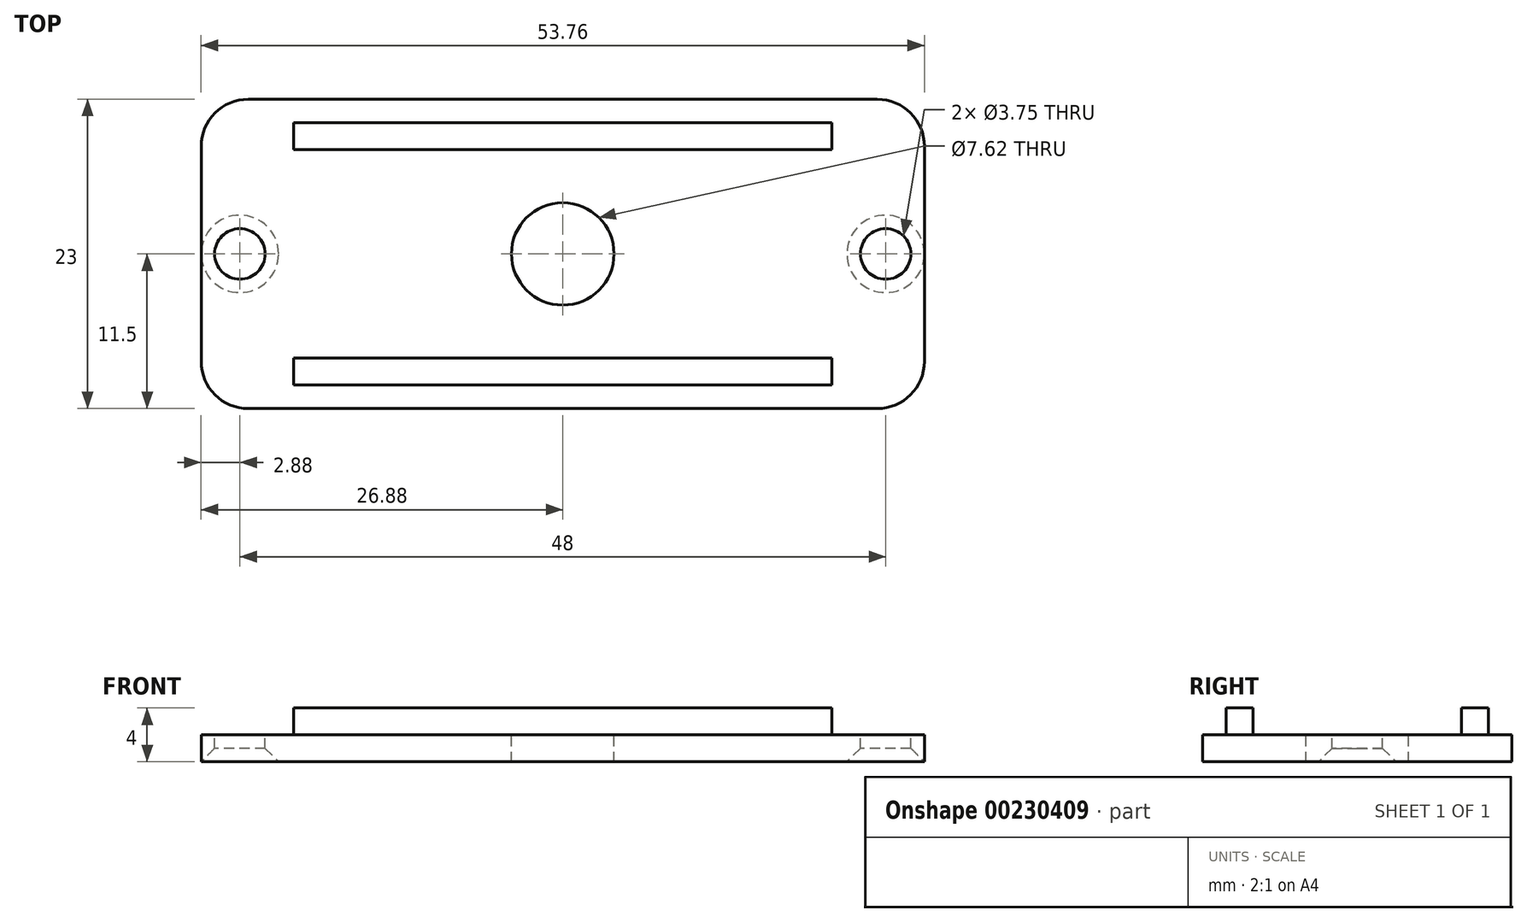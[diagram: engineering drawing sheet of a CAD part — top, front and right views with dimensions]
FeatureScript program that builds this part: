
annotation { "Feature Type Name" : "Feature", "Feature Type Description" : "" }
export const myFeature = defineFeature(function(context is Context, id is Id, definition is map)
    precondition{}
    {
        {
            var Q0;
            Q0=qCreatedBy(makeId("Top.planeOp"),FACE);
            var sketch = newSketch(context, id + "F0", { "sketchPlane" : qUnion([Q0])});
            skLineSegment(sketch, "E0.bottom", {"start": v(23.38, 11.5) * mm, "end": v(-23.37, 11.5) * mm});
            skLineSegment(sketch, "E0.top", {"start": v(23.38, -11.5) * mm, "end": v(-23.37, -11.5) * mm});
            skLineSegment(sketch, "E0.left", {"start": v(26.88, 8) * mm, "end": v(26.88, -8) * mm});
            skLineSegment(sketch, "E0.right", {"start": v(-26.87, 8) * mm, "end": v(-26.87, -8) * mm});
            skPoint(sketch, "E0.middle", {"position": v(0, 0) * mm});
            skPoint(sketch, "E1.visualSharp", {"position": v(-26.88, 11.5) * mm});
            skArc(sketch, "E1.filletArc", {"start": v(-23.37, 11.5) * mm, "mid": v(-25.85, 10.47) * mm, "end": v(-26.87, 8) * mm});
            skPoint(sketch, "E2.visualSharp", {"position": v(-26.87, -11.5) * mm});
            skArc(sketch, "E2.filletArc", {"start": v(-26.87, -8) * mm, "mid": v(-25.85, -10.47) * mm, "end": v(-23.37, -11.5) * mm});
            skPoint(sketch, "E3.visualSharp", {"position": v(26.88, -11.5) * mm});
            skArc(sketch, "E3.filletArc", {"start": v(23.38, -11.5) * mm, "mid": v(25.85, -10.47) * mm, "end": v(26.88, -8) * mm});
            skPoint(sketch, "E4.visualSharp", {"position": v(26.87, 11.5) * mm});
            skArc(sketch, "E4.filletArc", {"start": v(26.88, 8) * mm, "mid": v(25.85, 10.47) * mm, "end": v(23.38, 11.5) * mm});
            skSolve(sketch);
        }
        {
            var Q0;
            Q0=makeQuery(id+"F0.imprint","IMPRINT",FACE,{"disambiguationData":[TD([[makeQuery(id+"F0.imprint","IMPRINT",EDGE,{"derivedFrom":sQuery(id+"F0.wireOp",EDGE,"E0.bottom")}),1.0]])]});
            extrude(context, id + "F1", {"entities" : qUnion([Q0]), "depth" : 2 * mm});
        }
        {
            var Q0;
            Q0=makeQuery(id+"F1.opExtrude","CAP_FACE",FACE,{"disambiguationData":[OSD([sQuery(id+"F0.wireOp",EDGE,"E0.bottom"),sQuery(id+"F0.wireOp",EDGE,"E0.top"),sQuery(id+"F0.wireOp",EDGE,"E0.left"),sQuery(id+"F0.wireOp",EDGE,"E0.right"),sQuery(id+"F0.wireOp",EDGE,"E1.filletArc"),sQuery(id+"F0.wireOp",EDGE,"E2.filletArc"),sQuery(id+"F0.wireOp",EDGE,"E3.filletArc"),sQuery(id+"F0.wireOp",EDGE,"E4.filletArc")])],"isStart":false});
            var sketch = newSketch(context, id + "F2", { "sketchPlane" : qUnion([Q0])});
            skCircle(sketch, "E5", {"center": v(-24, 0) * mm, "radius": 1.88 * mm});
            skCircle(sketch, "E6", {"center": v(24, 0) * mm, "radius": 1.88 * mm});
            skSolve(sketch);
        }
        {
            var Q0;
            Q0 = qSketchRegion(id + "F2", true);
            extrude(context, id + "F3", {"entities" : qUnion([Q0]), "operationType" : NewBodyOperationType.REMOVE, "endBound" : BoundingType.THROUGH_ALL, "oppositeDirection" : true, "depth" : 25 * mm});
        }
        {
            var Q0;
            Q0=makeQuery(id+"F3.boolean.opBoolean","INTERSECT",EDGE,{"derivedFrom":[makeQuery(id+"F1.opExtrude","CAP_FACE",FACE,{"disambiguationData":[OSD([sQuery(id+"F0.wireOp",EDGE,"E0.bottom"),sQuery(id+"F0.wireOp",EDGE,"E0.top"),sQuery(id+"F0.wireOp",EDGE,"E0.left"),sQuery(id+"F0.wireOp",EDGE,"E0.right"),sQuery(id+"F0.wireOp",EDGE,"E1.filletArc"),sQuery(id+"F0.wireOp",EDGE,"E2.filletArc"),sQuery(id+"F0.wireOp",EDGE,"E3.filletArc"),sQuery(id+"F0.wireOp",EDGE,"E4.filletArc")])],"isStart":true}),makeQuery(id+"F3.opExtrude","SWEPT_FACE",FACE,{"disambiguationData":[OSD([sQuery(id+"F2.wireOp",EDGE,"E5")])]})]});
            var Q1;
            Q1=makeQuery(id+"F3.boolean.opBoolean","INTERSECT",EDGE,{"derivedFrom":[makeQuery(id+"F1.opExtrude","CAP_FACE",FACE,{"disambiguationData":[OSD([sQuery(id+"F0.wireOp",EDGE,"E0.bottom"),sQuery(id+"F0.wireOp",EDGE,"E0.top"),sQuery(id+"F0.wireOp",EDGE,"E0.left"),sQuery(id+"F0.wireOp",EDGE,"E0.right"),sQuery(id+"F0.wireOp",EDGE,"E1.filletArc"),sQuery(id+"F0.wireOp",EDGE,"E2.filletArc"),sQuery(id+"F0.wireOp",EDGE,"E3.filletArc"),sQuery(id+"F0.wireOp",EDGE,"E4.filletArc")])],"isStart":true}),makeQuery(id+"F3.opExtrude","SWEPT_FACE",FACE,{"disambiguationData":[OSD([sQuery(id+"F2.wireOp",EDGE,"E6")])]})]});
            chamfer(context, id + "F4", {"entities" : qUnion([Q0, Q1]), "width" : 1 * mm, "tangentPropagation" : true});
        }
        {
            var Q0;
            Q0=makeQuery(id+"F1.opExtrude","CAP_FACE",FACE,{"disambiguationData":[OSD([sQuery(id+"F0.wireOp",EDGE,"E0.bottom"),sQuery(id+"F0.wireOp",EDGE,"E0.top"),sQuery(id+"F0.wireOp",EDGE,"E0.left"),sQuery(id+"F0.wireOp",EDGE,"E0.right"),sQuery(id+"F0.wireOp",EDGE,"E1.filletArc"),sQuery(id+"F0.wireOp",EDGE,"E2.filletArc"),sQuery(id+"F0.wireOp",EDGE,"E3.filletArc"),sQuery(id+"F0.wireOp",EDGE,"E4.filletArc")])],"isStart":false});
            var sketch = newSketch(context, id + "F5", { "sketchPlane" : qUnion([Q0])});
            skLineSegment(sketch, "E7.bottom", {"start": v(20, 7.75) * mm, "end": v(-20, 7.75) * mm});
            skLineSegment(sketch, "E7.top", {"start": v(20, 9.75) * mm, "end": v(-20, 9.75) * mm});
            skLineSegment(sketch, "E7.left", {"start": v(20, 7.75) * mm, "end": v(20, 9.75) * mm});
            skLineSegment(sketch, "E7.right", {"start": v(-20, 7.75) * mm, "end": v(-20, 9.75) * mm});
            skPoint(sketch, "E7.middle", {"position": v(0, 8.75) * mm});
            skLineSegment(sketch, "E8.bottom", {"start": v(20, -9.75) * mm, "end": v(-20, -9.75) * mm});
            skLineSegment(sketch, "E8.top", {"start": v(20, -7.75) * mm, "end": v(-20, -7.75) * mm});
            skLineSegment(sketch, "E8.left", {"start": v(20, -9.75) * mm, "end": v(20, -7.75) * mm});
            skLineSegment(sketch, "E8.right", {"start": v(-20, -9.75) * mm, "end": v(-20, -7.75) * mm});
            skPoint(sketch, "E8.middle", {"position": v(0, -8.75) * mm});
            skSolve(sketch);
        }
        {
            var Q0;
            Q0 = qSketchRegion(id + "F5", true);
            extrude(context, id + "F6", {"entities" : qUnion([Q0]), "operationType" : NewBodyOperationType.ADD, "depth" : 2 * mm});
        }
        {
            var Q0;
            Q0=makeQuery(id+"F1.opExtrude","CAP_FACE",FACE,{"disambiguationData":[OSD([sQuery(id+"F0.wireOp",EDGE,"E0.bottom"),sQuery(id+"F0.wireOp",EDGE,"E0.top"),sQuery(id+"F0.wireOp",EDGE,"E0.left"),sQuery(id+"F0.wireOp",EDGE,"E0.right"),sQuery(id+"F0.wireOp",EDGE,"E1.filletArc"),sQuery(id+"F0.wireOp",EDGE,"E2.filletArc"),sQuery(id+"F0.wireOp",EDGE,"E3.filletArc"),sQuery(id+"F0.wireOp",EDGE,"E4.filletArc")])],"isStart":false});
            var sketch = newSketch(context, id + "F7", { "sketchPlane" : qUnion([Q0])});
            skCircle(sketch, "E9", {"center": v(0, 0) * mm, "radius": 3.81 * mm});
            skSolve(sketch);
        }
        {
            var Q0;
            Q0 = qSketchRegion(id + "F7", true);
            extrude(context, id + "F8", {"entities" : qUnion([Q0]), "operationType" : NewBodyOperationType.REMOVE, "endBound" : BoundingType.THROUGH_ALL, "oppositeDirection" : true, "depth" : 25 * mm});
        }
    });
